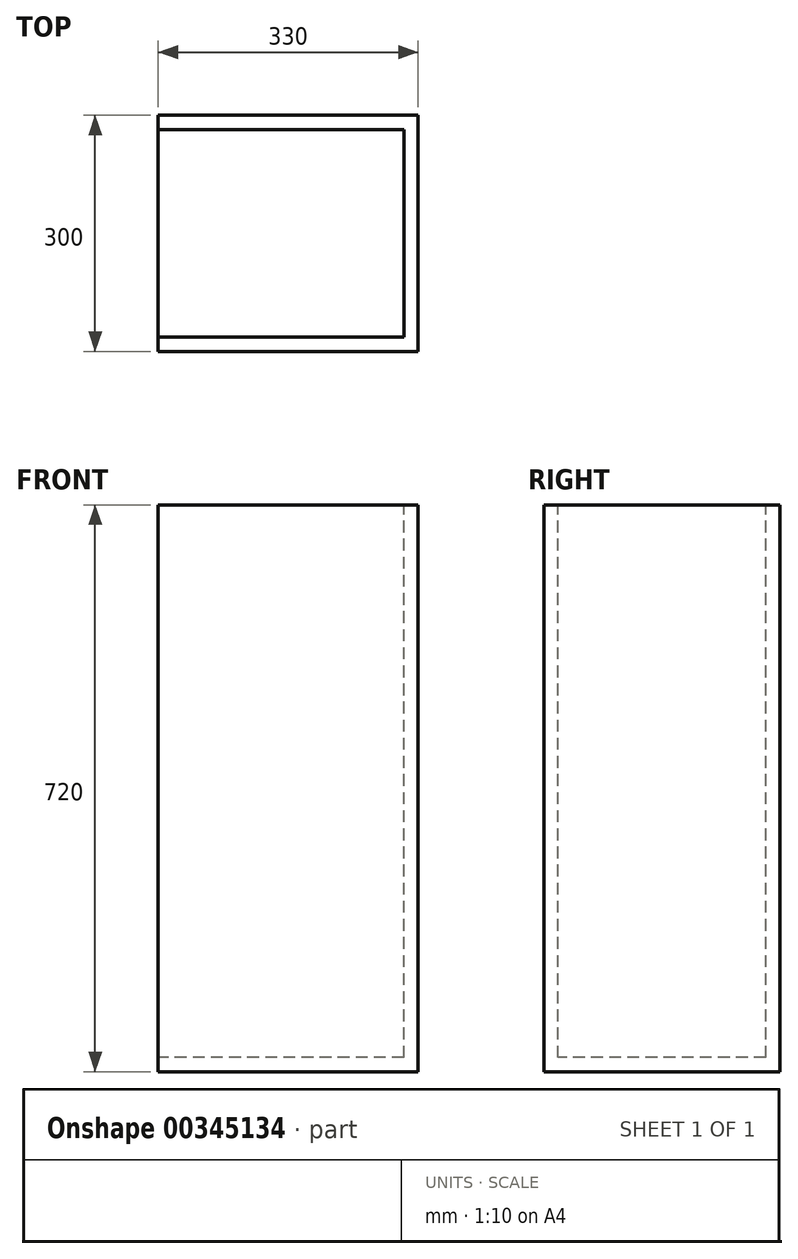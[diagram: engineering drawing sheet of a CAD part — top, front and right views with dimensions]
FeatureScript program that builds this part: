
annotation { "Feature Type Name" : "Feature", "Feature Type Description" : "" }
export const myFeature = defineFeature(function(context is Context, id is Id, definition is map)
    precondition{}
    {
        {
            var Q0;
            Q0=qCreatedBy(makeId("Right.planeOp"),FACE);
            var sketch = newSketch(context, id + "F0", { "sketchPlane" : qUnion([Q0])});
            skLineSegment(sketch, "E0.bottom", {"start": v(0, 0) * mm, "end": v(-42.14, 0) * mm});
            skLineSegment(sketch, "E0.top", {"start": v(0, 37.63) * mm, "end": v(-42.14, 37.63) * mm});
            skLineSegment(sketch, "E0.left", {"start": v(0, 0) * mm, "end": v(0, 37.63) * mm});
            skLineSegment(sketch, "E0.right", {"start": v(-42.14, 0) * mm, "end": v(-42.14, 37.63) * mm});
            skSolve(sketch);
        }
        {
            var Q0;
            Q0=makeQuery(id+"F0.imprint","IMPRINT",FACE,{"disambiguationData":[TD([[makeQuery(id+"F0.imprint","IMPRINT",EDGE,{"derivedFrom":sQuery(id+"F0.wireOp",EDGE,"E0.bottom")}),-1.0]])]});
            extrude(context, id + "F1", {"entities" : qUnion([Q0]), "depth" : 330 * mm});
        }
        {
            var Q0;
            Q0=makeQuery(id+"F1.opExtrude","SWEPT_FACE",FACE,{"disambiguationData":[OSD([sQuery(id+"F0.wireOp",EDGE,"E0.left")])]});
            extrude(context, id + "F2", {"entities" : qUnion([Q0]), "operationType" : NewBodyOperationType.ADD, "oppositeDirection" : true, "depth" : 300 * mm});
        }
        {
            var Q0;
            {var subQ0=sQuery(id+"F0.wireOp",EDGE,"E0.bottom");Q0=makeQuery(id+"F2.boolean.opBoolean","MERGE",FACE,{"derivedFrom":[makeQuery(id+"F1.opExtrude","SWEPT_FACE",FACE,{"disambiguationData":[OSD([subQ0])]}),makeQuery(id+"F2.opExtrude","SWEPT_FACE",FACE,{"disambiguationData":[OSD([subQ0,sQuery(id+"F0.wireOp",EDGE,"E0.left")])]})]});}
            extrude(context, id + "F3", {"entities" : qUnion([Q0]), "operationType" : NewBodyOperationType.ADD, "oppositeDirection" : true, "depth" : 720 * mm});
        }
        {
            var Q0;
            {var subQ0=sQuery(id+"F0.wireOp",EDGE,"E0.left");var subQ1=sQuery(id+"F0.wireOp",EDGE,"E0.bottom");Q0=makeQuery(id+"F3.boolean.opBoolean","MERGE",FACE,{"derivedFrom":[makeQuery(id+"F2.boolean.opBoolean","MERGE",FACE,{"derivedFrom":[makeQuery(id+"F1.opExtrude","CAP_FACE",FACE,{"disambiguationData":[OSD([subQ1,sQuery(id+"F0.wireOp",EDGE,"E0.top"),subQ0,sQuery(id+"F0.wireOp",EDGE,"E0.right")])],"isStart":true}),makeQuery(id+"F2.opExtrude","SWEPT_FACE",FACE,{"disambiguationData":[OSD([subQ0]),TDD([makeQuery(id+"F1.opExtrude","CAP_EDGE",EDGE,{"disambiguationData":[OSD([subQ0])],"isStart":true})])]})]}),makeQuery(id+"F3.opExtrude","SWEPT_FACE",FACE,{"disambiguationData":[OSD([subQ1,subQ0]),TDD([makeQuery(id+"F2.boolean.opBoolean","MERGE",EDGE,{"derivedFrom":[makeQuery(id+"F1.opExtrude","CAP_EDGE",EDGE,{"disambiguationData":[OSD([subQ1])],"isStart":true}),makeQuery(id+"F2.opExtrude","SWEPT_EDGE",EDGE,{"disambiguationData":[OSD([subQ1,subQ0]),TDD([makeQuery(id+"F1.opExtrude","CAP_VERTEX",VERTEX,{"disambiguationData":[OSD([subQ1,subQ0])],"isStart":true})])]})]})])]})]});}
            var Q1;
            Q1=makeQuery(id+"F3.opExtrude","CAP_FACE",FACE,{"disambiguationData":[OSD([sQuery(id+"F0.wireOp",EDGE,"E0.bottom"),sQuery(id+"F0.wireOp",EDGE,"E0.left")])],"isStart":false});
            shell(context, id + "F4", {"entities" : qUnion([Q0, Q1]), "thickness" : 18 * mm});
        }
    });
